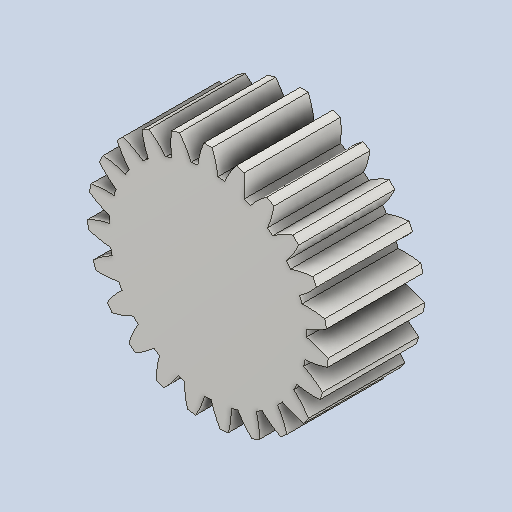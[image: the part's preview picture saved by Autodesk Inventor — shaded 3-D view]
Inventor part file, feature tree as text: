
AUTODESK INVENTOR PART (.ipt)
format: ipt  version: 2023 (Build 270158030, 158C)  size: 269,312 bytes
history: native  units: mm (DEFAULTED — no unit token found)
features: plane x3, other x3, sketch x2, extrude x1
ambient origin geometry x8: Origin, YZ Plane, XZ Plane, XY Plane, X Axis, Y Axis, Z Axis, Center Point
bodies: Solid1 (feature_tree)
feature tree (9):
  extrude  "Extrusion1"  Depth=20.0mm TaperAngle=0.0deg
  plane  "Work Plane2"
  plane  "Work Plane8"
  plane  "Work Plane9"
  other  "Spur Gear"
  sketch  "Sketch1"  dims[d0=50.0mm d1=20.0mm d2=0.0mm]
  sketch  "Sketch2"  dims[d3=46.0mm d4=10.0mm d5=0.0mm d16=80.0mm d17=0.0mm d34=1.36591mm d39=0.0mm d41=0.0mm d43=80.0mm d46=80.0mm d47=0.0mm d48=0.0mm]
  other  "Srf1"
  other  "Pitch Diameter"
